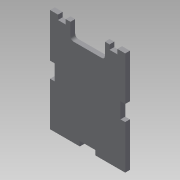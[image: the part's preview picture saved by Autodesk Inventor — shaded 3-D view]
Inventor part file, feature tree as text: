
AUTODESK INVENTOR PART (.ipt)
format: ipt  version: 2013 (Build 170138000, 138)  size: 118,272 bytes
history: native  units: mm
features: extrude x1
ambient origin geometry x8: Origin, YZ Plane, XZ Plane, XY Plane, X Axis, Y Axis, Z Axis, Center Point
bodies: Solid1 (feature_tree)
feature tree (1):
  extrude  "Extrusion1"  Depth=16.0mm
